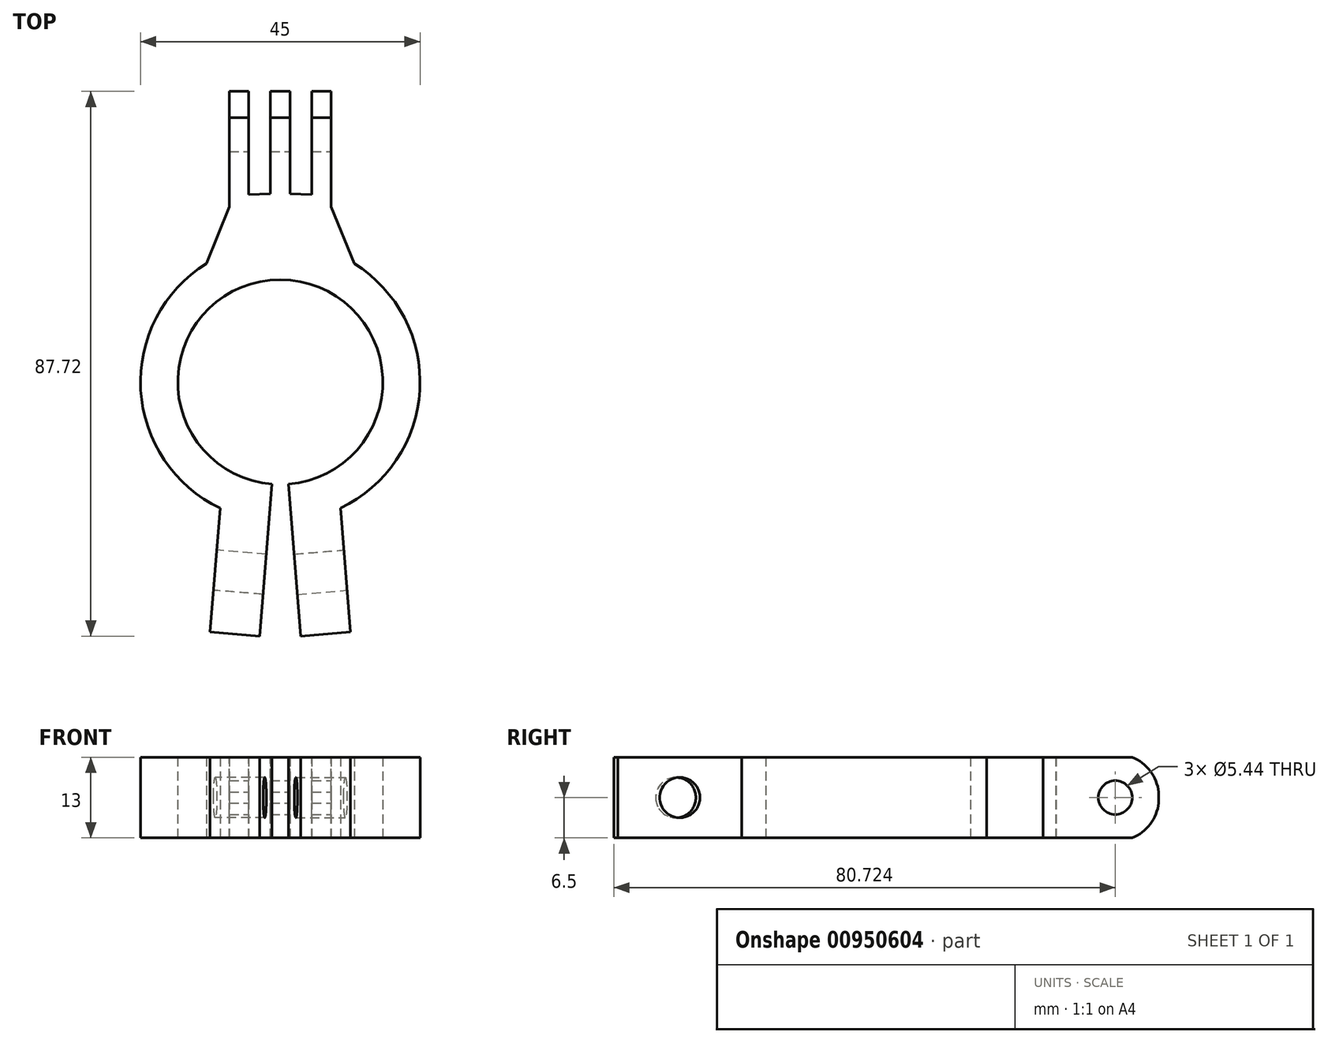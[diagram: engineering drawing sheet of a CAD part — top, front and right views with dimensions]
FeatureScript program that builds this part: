
annotation { "Feature Type Name" : "Feature", "Feature Type Description" : "" }
export const myFeature = defineFeature(function(context is Context, id is Id, definition is map)
    precondition{}
    {
        {
            var Q0;
            Q0=qCreatedBy(makeId("Top.planeOp"),FACE);
            var sketch = newSketch(context, id + "F0", { "sketchPlane" : qUnion([Q0])});
            skArc(sketch, "E0", {"start": v(9.67, -20.32) * mm, "mid": v(0, 22.5) * mm, "end": v(-9.67, -20.32) * mm});
            skArc(sketch, "E1", {"start": v(1.33, -16.45) * mm, "mid": v(0, 16.5) * mm, "end": v(-1.33, -16.45) * mm});
            skLineSegment(sketch, "E2", {"start": v(-1.82, -22.43) * mm, "end": v(-3.31, -40.9) * mm});
            skLineSegment(sketch, "E3.MirrorCS", {"start": v(1.82, -22.43) * mm, "end": v(3.31, -40.9) * mm});
            skLineSegment(sketch, "E4", {"start": v(-1.33, -16.45) * mm, "end": v(-3.31, -40.9) * mm});
            skLineSegment(sketch, "E5", {"start": v(-3.31, -40.9) * mm, "end": v(-11.29, -40.25) * mm});
            skLineSegment(sketch, "E6", {"start": v(-11.29, -40.25) * mm, "end": v(-9.67, -20.32) * mm});
            skLineSegment(sketch, "E7.MirrorCS", {"start": v(3.31, -40.9) * mm, "end": v(11.29, -40.25) * mm});
            skLineSegment(sketch, "E8.MirrorCS", {"start": v(11.29, -40.25) * mm, "end": v(9.67, -20.32) * mm});
            skPoint(sketch, "E9.orphan", {"position": v(-6.17, -76.18) * mm});
            skPoint(sketch, "E10.orphan", {"position": v(6.17, -76.18) * mm});
            skPoint(sketch, "E11.orphan", {"position": v(13.38, -60.45) * mm});
            skPoint(sketch, "E12.orphan", {"position": v(-12.1, -60.45) * mm});
            skLineSegment(sketch, "E13", {"start": v(1.33, -16.45) * mm, "end": v(1.82, -22.43) * mm});
            skPoint(sketch, "E14.orphan", {"position": v(9.14, -13.74) * mm});
            skPoint(sketch, "E15.orphan", {"position": v(-9.14, -13.74) * mm});
            skLineSegment(sketch, "E16.bottom", {"start": v(-8.2, 46.82) * mm, "end": v(-5.1, 46.82) * mm});
            skLineSegment(sketch, "E16.left", {"start": v(-8.2, 46.82) * mm, "end": v(-8.2, 20.96) * mm});
            skLineSegment(sketch, "E16.right", {"start": v(8.2, 46.82) * mm, "end": v(8.2, 20.96) * mm});
            skPoint(sketch, "E17.orphan", {"position": v(8.2, -46.82) * mm});
            skPoint(sketch, "E18.orphan", {"position": v(-8.2, -46.82) * mm});
            skLineSegment(sketch, "E19.left", {"start": v(-8.2, 46.82) * mm, "end": v(-8.2, 33.14) * mm});
            skLineSegment(sketch, "E19.right", {"start": v(-5.1, 46.82) * mm, "end": v(-5.1, 30.22) * mm});
            skLineSegment(sketch, "E20.MirrorCS", {"start": v(5.1, 46.82) * mm, "end": v(5.1, 30.22) * mm});
            skLineSegment(sketch, "E21", {"start": v(-1.6, 46.82) * mm, "end": v(-1.6, 30.3) * mm});
            skLineSegment(sketch, "E22", {"start": v(0, 33.22) * mm, "end": v(0, 46.82) * mm});
            skLineSegment(sketch, "E23.MirrorCS", {"start": v(1.6, 46.82) * mm, "end": v(1.6, 30.3) * mm});
            skPoint(sketch, "E24.MirrorCS.end.orphan", {"position": v(5.1, 30.22) * mm});
            skPoint(sketch, "E24.MirrorCS.start.orphan", {"position": v(8.2, 33.14) * mm});
            skLineSegment(sketch, "E25.trimOffspring", {"start": v(5.1, 46.82) * mm, "end": v(8.2, 46.82) * mm});
            skLineSegment(sketch, "E26.trimOffspring", {"start": v(-1.6, 46.82) * mm, "end": v(1.6, 46.82) * mm});
            skPoint(sketch, "E27.MirrorCS.end.orphan", {"position": v(0, 33.22) * mm});
            skPoint(sketch, "E27.MirrorCS.start.orphan", {"position": v(1.6, 30.3) * mm});
            skLineSegment(sketch, "E28", {"start": v(-5.1, 30.22) * mm, "end": v(-1.6, 30.3) * mm});
            skLineSegment(sketch, "E29", {"start": v(1.6, 30.3) * mm, "end": v(5.1, 30.22) * mm});
            skLineSegment(sketch, "E30", {"start": v(-8.2, 30.25) * mm, "end": v(8.2, 30.25) * mm, "construction": true});
            skLineSegment(sketch, "E31", {"start": v(0, 22.5) * mm, "end": v(0, 30.25) * mm, "construction": true});
            skLineSegment(sketch, "E32", {"start": v(-3.52, 30.25) * mm, "end": v(-3.52, 47.25) * mm, "construction": true});
            skLineSegment(sketch, "E33", {"start": v(-8.2, 28.22) * mm, "end": v(-11.9, 19.09) * mm});
            skLineSegment(sketch, "E34.MirrorCS", {"start": v(8.2, 28.22) * mm, "end": v(11.9, 19.09) * mm});
            skSolve(sketch);
        }
        {
            var Q0;
            Q0 = qSketchRegion(id + "F0", true);
            extrude(context, id + "F1", {"entities" : qUnion([Q0]), "depth" : 13 * mm, "offsetDistance" : 25 * mm});
        }
        {
            var Q0;
            Q0=makeQuery(id+"F1.opExtrude","SWEPT_FACE",FACE,{"disambiguationData":[OSD([sQuery(id+"F0.wireOp",EDGE,"E16.right")])]});
            var sketch = newSketch(context, id + "F2", { "sketchPlane" : qUnion([Q0])});
            skLineSegment(sketch, "E35", {"start": v(46.82, 6.5) * mm, "end": v(39.82, 6.5) * mm, "construction": true});
            skCircle(sketch, "E36", {"center": v(39.82, 6.5) * mm, "radius": 2.72 * mm});
            skCircle(sketch, "E37", {"center": v(39.82, 6.5) * mm, "radius": 7.05 * mm});
            skLineSegment(sketch, "E38", {"start": v(46.82, 6.5) * mm, "end": v(46.82, 13) * mm});
            skLineSegment(sketch, "E39", {"start": v(46.82, 13) * mm, "end": v(42.56, 13) * mm});
            skLineSegment(sketch, "E40", {"start": v(46.82, 6.5) * mm, "end": v(46.82, 0) * mm});
            skLineSegment(sketch, "E41", {"start": v(46.82, 0) * mm, "end": v(42.56, 0) * mm});
            skSolve(sketch);
        }
        {
            var Q0;
            {var subQ0=sQuery(id+"F2.wireOp",EDGE,"E39");Q0=makeQuery(id+"F2.imprint","IMPRINT",FACE,{"disambiguationData":[TD([[makeQuery(id+"F2.imprint","IMPRINT",EDGE,{"derivedFrom":subQ0}),1.0]])]});}
            var Q1;
            {var subQ0=sQuery(id+"F2.wireOp",EDGE,"E41");Q1=makeQuery(id+"F2.imprint","IMPRINT",FACE,{"disambiguationData":[TD([[makeQuery(id+"F2.imprint","IMPRINT",EDGE,{"derivedFrom":subQ0}),-1.0]])]});}
            extrude(context, id + "F3", {"entities" : qUnion([Q0, Q1]), "operationType" : NewBodyOperationType.REMOVE, "oppositeDirection" : true, "depth" : 17 * mm, "offsetDistance" : 25 * mm});
        }
        {
            var Q0;
            Q0=makeQuery(id+"F2.imprint","IMPRINT",FACE,{"disambiguationData":[TD([[makeQuery(id+"F2.imprint","IMPRINT",EDGE,{"derivedFrom":sQuery(id+"F2.wireOp",EDGE,"E36")}),1.0]])]});
            extrude(context, id + "F4", {"entities" : qUnion([Q0]), "operationType" : NewBodyOperationType.REMOVE, "oppositeDirection" : true, "depth" : 17 * mm, "offsetDistance" : 25 * mm});
        }
        {
            var Q0;
            Q0=makeQuery(id+"F1.opExtrude","SWEPT_FACE",FACE,{"disambiguationData":[OSD([sQuery(id+"F0.wireOp",EDGE,"E8.MirrorCS")])]});
            var sketch = newSketch(context, id + "F5", { "sketchPlane" : qUnion([Q0])});
            skLineSegment(sketch, "E42", {"start": v(-41.03, 13) * mm, "end": v(-21.03, 0) * mm, "construction": true});
            skLineSegment(sketch, "E43", {"start": v(-21.03, 0) * mm, "end": v(-41.03, 0) * mm});
            skLineSegment(sketch, "E44", {"start": v(-41.03, 0) * mm, "end": v(-21.03, 13) * mm, "construction": true});
            skCircle(sketch, "E45", {"center": v(-31.03, 6.5) * mm, "radius": 3.25 * mm});
            skSolve(sketch);
        }
        {
            var Q0;
            Q0=makeQuery(id+"F5.imprint","IMPRINT",FACE,{"disambiguationData":[TD([[makeQuery(id+"F5.imprint","IMPRINT",EDGE,{"derivedFrom":sQuery(id+"F5.wireOp",EDGE,"E45")}),1.0]])]});
            extrude(context, id + "F6", {"entities" : qUnion([Q0]), "operationType" : NewBodyOperationType.REMOVE, "oppositeDirection" : true, "depth" : 13 * mm, "offsetDistance" : 25 * mm});
        }
        {
            var Q0;
            Q0=makeQuery(id+"F1.opExtrude","SWEPT_FACE",FACE,{"disambiguationData":[OSD([sQuery(id+"F0.wireOp",EDGE,"E6")])]});
            var sketch = newSketch(context, id + "F7", { "sketchPlane" : qUnion([Q0])});
            skLineSegment(sketch, "E46", {"start": v(21.03, 0) * mm, "end": v(41.03, 13) * mm, "construction": true});
            skCircle(sketch, "E47", {"center": v(31.03, 6.5) * mm, "radius": 3.25 * mm});
            skSolve(sketch);
        }
        {
            var Q0;
            Q0=makeQuery(id+"F7.imprint","IMPRINT",FACE,{"disambiguationData":[TD([[makeQuery(id+"F7.imprint","IMPRINT",EDGE,{"derivedFrom":sQuery(id+"F7.wireOp",EDGE,"E47")}),1.0]])]});
            extrude(context, id + "F8", {"entities" : qUnion([Q0]), "operationType" : NewBodyOperationType.REMOVE, "oppositeDirection" : true, "depth" : 13 * mm, "offsetDistance" : 25 * mm});
        }
    });
